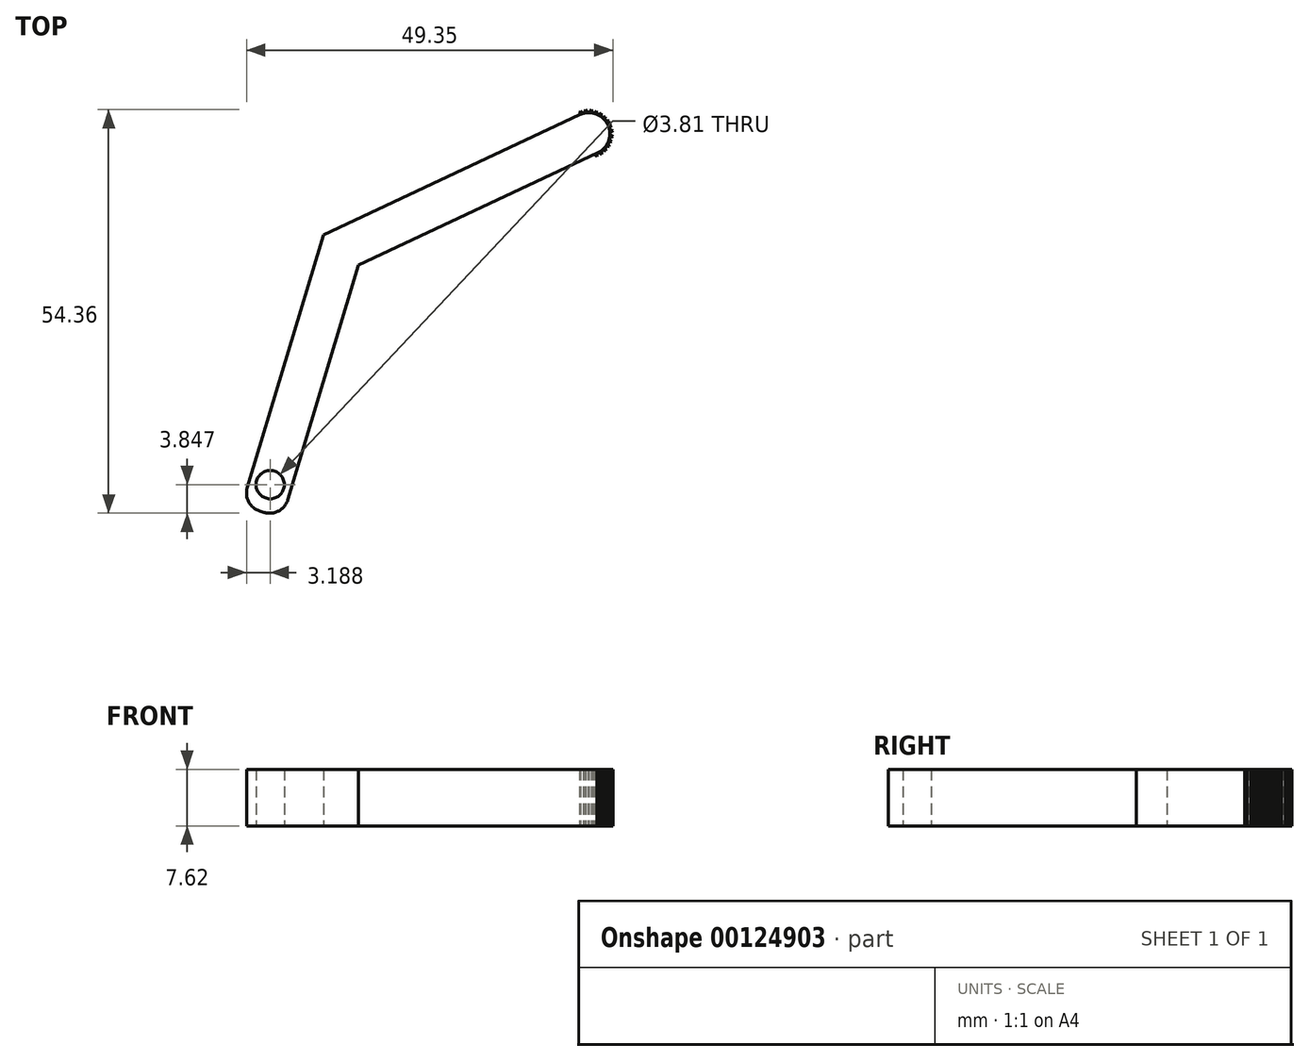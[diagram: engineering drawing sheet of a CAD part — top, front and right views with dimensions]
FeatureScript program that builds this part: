
annotation { "Feature Type Name" : "Feature", "Feature Type Description" : "" }
export const myFeature = defineFeature(function(context is Context, id is Id, definition is map)
    precondition{}
    {
        {
            var Q0;
            Q0=qCreatedBy(makeId("Top.planeOp"),FACE);
            var sketch = newSketch(context, id + "F0", { "sketchPlane" : qUnion([Q0])});
            skLineSegment(sketch, "E0", {"start": v(0, 0) * mm, "end": v(11.01, 36.47) * mm});
            skLineSegment(sketch, "E1", {"start": v(11.01, 36.47) * mm, "end": v(45.5, 52.65) * mm});
            skLineSegment(sketch, "E2", {"start": v(45.5, 52.65) * mm, "end": v(47.93, 47.5) * mm});
            skLineSegment(sketch, "E3", {"start": v(47.93, 47.5) * mm, "end": v(15.73, 32.4) * mm});
            skLineSegment(sketch, "E4", {"start": v(15.73, 32.4) * mm, "end": v(5.45, -1.65) * mm});
            skLineSegment(sketch, "E5", {"start": v(5.45, -1.65) * mm, "end": v(0, 0) * mm});
            skCircle(sketch, "E6", {"center": v(46.72, 50.08) * mm, "radius": 2.85 * mm});
            skLineSegment(sketch, "E7", {"start": v(45.5, 52.65) * mm, "end": v(45.6, 53.16) * mm});
            skLineSegment(sketch, "E8", {"start": v(45.6, 53.16) * mm, "end": v(45.98, 52.83) * mm});
            skLineSegment(sketch, "E9", {"start": v(45.5, 52.65) * mm, "end": v(45.98, 52.83) * mm});
            skLineSegment(sketch, "E10", {"start": v(2.73, -0.82) * mm, "end": v(3.82, 2.83) * mm});
            skCircle(sketch, "E11", {"center": v(3.82, 2.83) * mm, "radius": 1.9 * mm});
            skSolve(sketch);
        }
        {
            var Q0;
            {var subQ5=sQuery(id+"F0.wireOp",EDGE,"E0");Q0=makeQuery(id+"F0.imprint","IMPRINT",FACE,{"disambiguationData":[TD([[makeQuery(id+"F0.imprint","IMPRINT",EDGE,{"derivedFrom":subQ5}),-1.0]])]});}
            var Q1;
            {var subQ0=sQuery(id+"F0.wireOp",EDGE,"E2");Q1=makeQuery(id+"F0.imprint","IMPRINT",FACE,{"disambiguationData":[TD([[makeQuery(id+"F0.imprint","IMPRINT",EDGE,{"derivedFrom":subQ0}),-1.0]])]});}
            var Q2;
            {var subQ0=sQuery(id+"F0.wireOp",EDGE,"E2");Q2=makeQuery(id+"F0.imprint","IMPRINT",FACE,{"disambiguationData":[TD([[makeQuery(id+"F0.imprint","IMPRINT",EDGE,{"derivedFrom":subQ0}),1.0]])]});}
            var Q3;
            {var subQ1=sQuery(id+"F0.wireOp",EDGE,"E7");Q3=makeQuery(id+"F0.imprint","IMPRINT",FACE,{"disambiguationData":[TD([[makeQuery(id+"F0.imprint","IMPRINT",EDGE,{"derivedFrom":subQ1}),-1.0]])]});}
            extrude(context, id + "F1", {"entities" : qUnion([Q0, Q1, Q2, Q3]), "depth" : 7.62 * mm});
        }
        {
            var Q0;
            Q0=makeQuery(id+"F1.opExtrude","CAP_FACE",FACE,{"disambiguationData":[OSD([sQuery(id+"F0.wireOp",EDGE,"E0"),sQuery(id+"F0.wireOp",EDGE,"E1"),sQuery(id+"F0.wireOp",EDGE,"E3"),sQuery(id+"F0.wireOp",EDGE,"E4"),sQuery(id+"F0.wireOp",EDGE,"E5"),sQuery(id+"F0.wireOp",EDGE,"E6"),sQuery(id+"F0.wireOp",EDGE,"E9"),sQuery(id+"F0.wireOp",EDGE,"E11")])],"isStart":false});
            var sketch = newSketch(context, id + "F2", { "sketchPlane" : qUnion([Q0])});
            skLineSegment(sketch, "E12", {"start": v(45.5, 52.65) * mm, "end": v(47.93, 47.5) * mm});
            skSolve(sketch);
        }
        {
            var Q0;
            Q0=makeQuery(id+"F2.imprint","IMPRINT",FACE,{"disambiguationData":[TD([[makeQuery(id+"F2.imprint","IMPRINT",EDGE,{"derivedFrom":sQuery(id+"F2.wireOp",EDGE,"E12")}),1.0]])]});
            extrude(context, id + "F3", {"entities" : qUnion([Q0]), "operationType" : NewBodyOperationType.ADD, "depth" : 2.54 * mm});
        }
        {
            var Q0;
            Q0=makeQuery(id+"F3.opExtrude","SWEPT_FACE",FACE,{"disambiguationData":[OSD([sQuery(id+"F2.wireOp",EDGE,"E12")])]});
            var sketch = newSketch(context, id + "F4", { "sketchPlane" : qUnion([Q0])});
            skLineSegment(sketch, "E13", {"start": v(-25.5, 10.16) * mm, "end": v(-25.5, 7.62) * mm});
            skLineSegment(sketch, "E14.1.0", {"start": v(3.95, -27.16) * mm, "end": v(6.15, -25.89) * mm});
            skLineSegment(sketch, "E14.2.0", {"start": v(21.55, 17) * mm, "end": v(19.35, 18.27) * mm});
            skPoint(sketch, "E14.center", {"position": v(0, 0) * mm});
            skSolve(sketch);
        }
        {
            var Q0;
            Q0=makeQuery(id+"F1.opExtrude","SWEPT_BODY",BODY,{"disambiguationData":[OSD([sQuery(id+"F0.wireOp",EDGE,"E6"),sQuery(id+"F0.wireOp",EDGE,"E7"),sQuery(id+"F0.wireOp",EDGE,"E8")])]});
            var Q1;
            Q1=sQuery(id+"F4.wireOp",EDGE,"E13");
            circularPattern(context, id + "F5", {"entities" : qUnion([Q0]), "axis" : qUnion([Q1]), "angle" : 180 * degree, "instanceCount" : 15, "equalSpace" : true});
        }
        {
            var Q0;
            Q0=makeQuery(id+"F3.opExtrude","CAP_FACE",FACE,{"disambiguationData":[OSD([sQuery(id+"F0.wireOp",EDGE,"E6"),sQuery(id+"F0.wireOp",EDGE,"E9"),sQuery(id+"F2.wireOp",EDGE,"E12")])],"isStart":false});
            extrude(context, id + "F6", {"entities" : qUnion([Q0]), "operationType" : NewBodyOperationType.REMOVE, "oppositeDirection" : true, "depth" : 2.54 * mm});
        }
        {
            var Q0;
            Q0=makeQuery(id+"F1.opExtrude","SWEPT_EDGE",EDGE,{"disambiguationData":[OSD([sQuery(id+"F0.wireOp",EDGE,"E4"),sQuery(id+"F0.wireOp",EDGE,"E5")])]});
            var Q1;
            Q1=makeQuery(id+"F1.opExtrude","SWEPT_EDGE",EDGE,{"disambiguationData":[OSD([sQuery(id+"F0.wireOp",EDGE,"E0"),sQuery(id+"F0.wireOp",EDGE,"E5")])]});
            fillet(context, id + "F7", {"entities" : qUnion([Q0, Q1]), "radius" : 2.54 * mm, "tangentPropagation" : true, "allowEdgeOverflow" : false});
        }
    });
